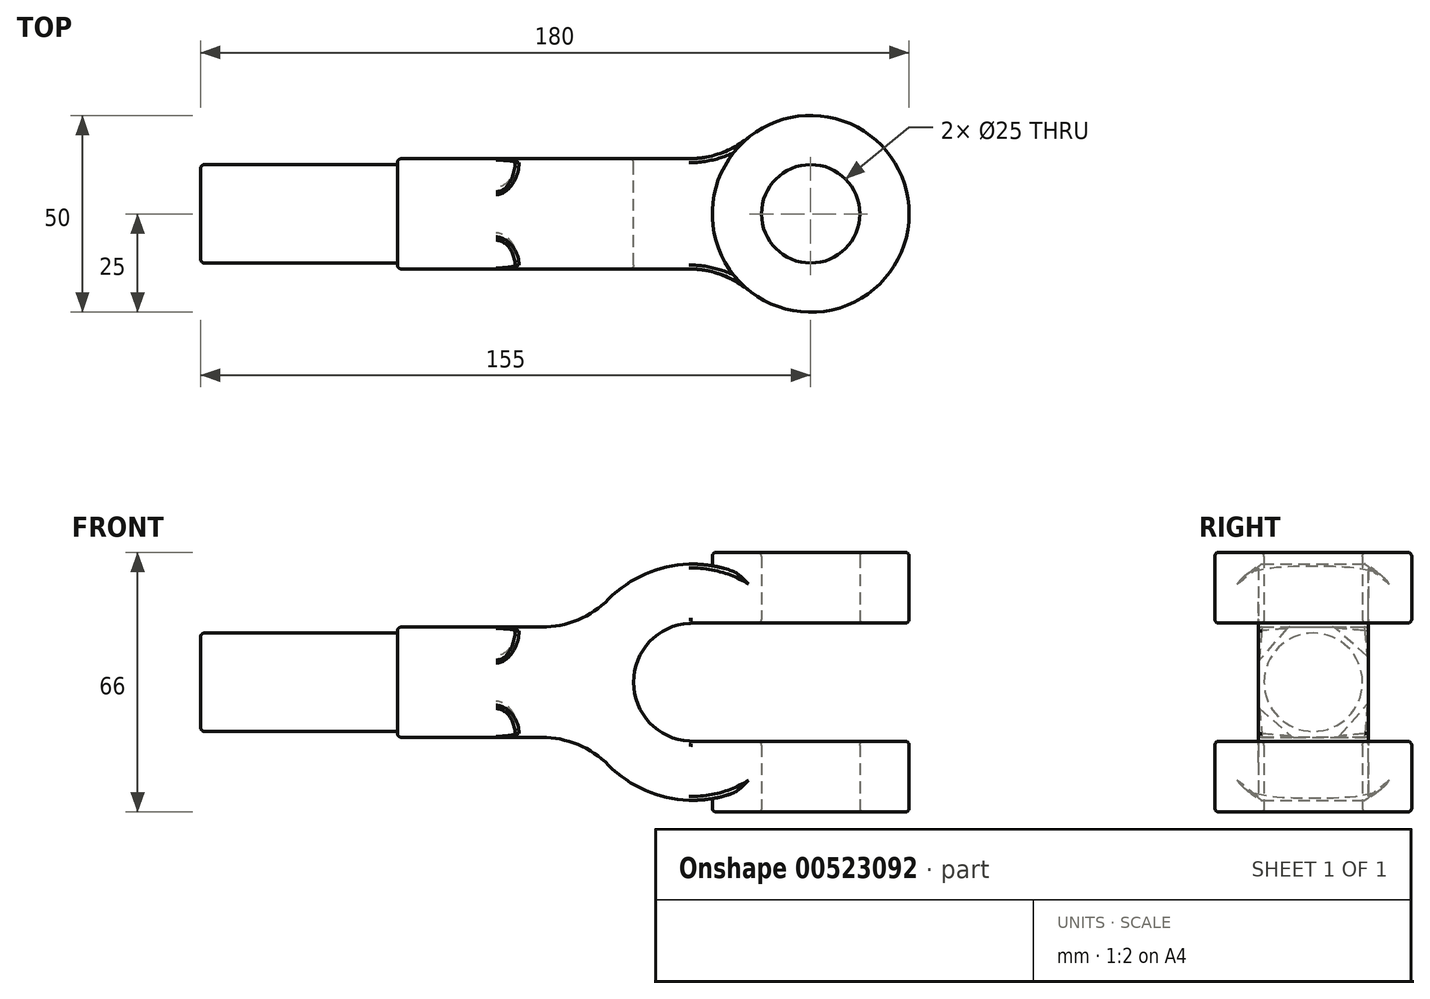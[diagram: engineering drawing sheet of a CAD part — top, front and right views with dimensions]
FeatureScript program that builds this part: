
annotation { "Feature Type Name" : "Feature", "Feature Type Description" : "" }
export const myFeature = defineFeature(function(context is Context, id is Id, definition is map)
    precondition{}
    {
        {
            var Q0;
            Q0=qCreatedBy(makeId("Top.planeOp"),FACE);
            var sketch = newSketch(context, id + "F0", { "sketchPlane" : qUnion([Q0])});
            skCircle(sketch, "E0", {"center": v(0, 0) * mm, "radius": 25 * mm});
            skSolve(sketch);
        }
        {
            var Q0;
            Q0 = qSketchRegion(id + "F0", true);
            extrude(context, id + "F1", {"entities" : qUnion([Q0]), "endBound" : BoundingType.SYMMETRIC, "depth" : 66 * mm, "offsetDistance" : 25 * mm});
        }
        {
            var Q0;
            Q0=qCreatedBy(makeId("Front.planeOp"),FACE);
            var sketch = newSketch(context, id + "F2", { "sketchPlane" : qUnion([Q0])});
            skArc(sketch, "E1", {"start": v(-56.53, -14) * mm, "mid": v(0, 0) * mm, "end": v(-56.53, 14) * mm});
            skCircle(sketch, "E2", {"center": v(-30, 0) * mm, "radius": 15 * mm});
            skLineSegment(sketch, "E3.bottom", {"start": v(-75, 14) * mm, "end": v(-65, 14) * mm});
            skLineSegment(sketch, "E3.top", {"start": v(-75, -14) * mm, "end": v(-56.53, -14) * mm});
            skLineSegment(sketch, "E3.left", {"start": v(-75, 14) * mm, "end": v(-75, -14) * mm});
            skLineSegment(sketch, "E4", {"start": v(-65, 14) * mm, "end": v(-56.53, 14) * mm});
            skPoint(sketch, "E5.orphan", {"position": v(-55, 14) * mm});
            skSolve(sketch);
        }
        {
            var Q0;
            Q0 = qSketchRegion(id + "F2", true);
            extrude(context, id + "F3", {"entities" : qUnion([Q0]), "operationType" : NewBodyOperationType.ADD, "endBound" : BoundingType.SYMMETRIC, "depth" : 28 * mm, "offsetDistance" : 25 * mm});
        }
        {
            var Q0;
            Q0=makeQuery(id+"F3.opExtrude","SWEPT_FACE",FACE,{"disambiguationData":[OSD([sQuery(id+"F2.wireOp",EDGE,"E3.left")])]});
            extrude(context, id + "F4", {"entities" : qUnion([Q0]), "operationType" : NewBodyOperationType.ADD, "depth" : 30 * mm, "offsetDistance" : 25 * mm});
        }
        {
            var Q0;
            Q0=makeQuery(id+"F4.opExtrude","CAP_FACE",FACE,{"disambiguationData":[OSD([sQuery(id+"F2.wireOp",EDGE,"E3.left")])],"isStart":false});
            var sketch = newSketch(context, id + "F5", { "sketchPlane" : qUnion([Q0])});
            skCircle(sketch, "E6", {"center": v(0, 0) * mm, "radius": 12.5 * mm});
            skSolve(sketch);
        }
        {
            var Q0;
            Q0 = qSketchRegion(id + "F5", true);
            extrude(context, id + "F6", {"entities" : qUnion([Q0]), "operationType" : NewBodyOperationType.ADD, "depth" : 50 * mm, "offsetDistance" : 25 * mm});
        }
        {
            var Q0;
            Q0=qCreatedBy(makeId("Front.planeOp"),FACE);
            var sketch = newSketch(context, id + "F7", { "sketchPlane" : qUnion([Q0])});
            skLineSegment(sketch, "E7.bottom", {"start": v(-30, 15) * mm, "end": v(30, 15) * mm});
            skLineSegment(sketch, "E7.top", {"start": v(-30, -15) * mm, "end": v(30, -15) * mm});
            skLineSegment(sketch, "E7.left", {"start": v(-30, 15) * mm, "end": v(-30, -15) * mm});
            skLineSegment(sketch, "E7.right", {"start": v(30, 15) * mm, "end": v(30, -15) * mm});
            skPoint(sketch, "E7.middle", {"position": v(0, 0) * mm});
            skSolve(sketch);
        }
        {
            var Q0;
            Q0 = qSketchRegion(id + "F7", true);
            extrude(context, id + "F8", {"entities" : qUnion([Q0]), "operationType" : NewBodyOperationType.REMOVE, "endBound" : BoundingType.SYMMETRIC, "oppositeDirection" : true, "depth" : 60 * mm, "offsetDistance" : 25 * mm});
        }
        {
            var Q0;
            Q0=makeQuery(id+"F1.opExtrude","CAP_FACE",FACE,{"disambiguationData":[OSD([sQuery(id+"F0.wireOp",EDGE,"E0")])],"isStart":true});
            var sketch = newSketch(context, id + "F9", { "sketchPlane" : qUnion([Q0])});
            skCircle(sketch, "E8", {"center": v(0, 0) * mm, "radius": 12.5 * mm});
            skSolve(sketch);
        }
        {
            var Q0;
            Q0 = qSketchRegion(id + "F9", true);
            extrude(context, id + "F10", {"entities" : qUnion([Q0]), "operationType" : NewBodyOperationType.REMOVE, "endBound" : BoundingType.THROUGH_ALL, "oppositeDirection" : true, "depth" : 25 * mm, "offsetDistance" : 25 * mm});
        }
        {
            var Q0;
            Q0=makeQuery(id+"F3.boolean.opBoolean","INTERSECT",EDGE,{"disambiguationData":[OD(1.0)],"derivedFrom":[makeQuery(id+"F1.opExtrude","SWEPT_FACE",FACE,{"disambiguationData":[OSD([sQuery(id+"F0.wireOp",EDGE,"E0")])]}),makeQuery(id+"F3.opExtrude","CAP_FACE",FACE,{"disambiguationData":[OSD([sQuery(id+"F2.wireOp",EDGE,"E1"),sQuery(id+"F2.wireOp",EDGE,"E2"),sQuery(id+"F2.wireOp",EDGE,"E3.bottom"),sQuery(id+"F2.wireOp",EDGE,"E3.top"),sQuery(id+"F2.wireOp",EDGE,"E3.left"),sQuery(id+"F2.wireOp",EDGE,"E4")])],"isStart":false})]});
            fillet(context, id + "F11", {"entities" : qUnion([Q0]), "radius" : 24 * mm, "tangentPropagation" : true, "allowEdgeOverflow" : false});
        }
        {
            var Q0;
            Q0=makeQuery(id+"F3.boolean.opBoolean","INTERSECT",EDGE,{"disambiguationData":[OD(0.0)],"derivedFrom":[makeQuery(id+"F1.opExtrude","SWEPT_FACE",FACE,{"disambiguationData":[OSD([sQuery(id+"F0.wireOp",EDGE,"E0")])]}),makeQuery(id+"F3.opExtrude","CAP_FACE",FACE,{"disambiguationData":[OSD([sQuery(id+"F2.wireOp",EDGE,"E1"),sQuery(id+"F2.wireOp",EDGE,"E2"),sQuery(id+"F2.wireOp",EDGE,"E3.bottom"),sQuery(id+"F2.wireOp",EDGE,"E3.top"),sQuery(id+"F2.wireOp",EDGE,"E3.left"),sQuery(id+"F2.wireOp",EDGE,"E4")])],"isStart":false})]});
            fillet(context, id + "F12", {"entities" : qUnion([Q0]), "radius" : 24 * mm, "tangentPropagation" : true, "allowEdgeOverflow" : false});
        }
        {
            var Q0;
            Q0=makeQuery(id+"F3.boolean.opBoolean","INTERSECT",EDGE,{"disambiguationData":[OD(0.0)],"derivedFrom":[makeQuery(id+"F1.opExtrude","SWEPT_FACE",FACE,{"disambiguationData":[OSD([sQuery(id+"F0.wireOp",EDGE,"E0")])]}),makeQuery(id+"F3.opExtrude","CAP_FACE",FACE,{"disambiguationData":[OSD([sQuery(id+"F2.wireOp",EDGE,"E1"),sQuery(id+"F2.wireOp",EDGE,"E2"),sQuery(id+"F2.wireOp",EDGE,"E3.bottom"),sQuery(id+"F2.wireOp",EDGE,"E3.top"),sQuery(id+"F2.wireOp",EDGE,"E3.left"),sQuery(id+"F2.wireOp",EDGE,"E4")])],"isStart":true})]});
            fillet(context, id + "F13", {"entities" : qUnion([Q0]), "radius" : 24 * mm, "tangentPropagation" : true, "allowEdgeOverflow" : false});
        }
        {
            var Q0;
            Q0=makeQuery(id+"F3.boolean.opBoolean","INTERSECT",EDGE,{"disambiguationData":[OD(1.0)],"derivedFrom":[makeQuery(id+"F1.opExtrude","SWEPT_FACE",FACE,{"disambiguationData":[OSD([sQuery(id+"F0.wireOp",EDGE,"E0")])]}),makeQuery(id+"F3.opExtrude","CAP_FACE",FACE,{"disambiguationData":[OSD([sQuery(id+"F2.wireOp",EDGE,"E1"),sQuery(id+"F2.wireOp",EDGE,"E2"),sQuery(id+"F2.wireOp",EDGE,"E3.bottom"),sQuery(id+"F2.wireOp",EDGE,"E3.top"),sQuery(id+"F2.wireOp",EDGE,"E3.left"),sQuery(id+"F2.wireOp",EDGE,"E4")])],"isStart":true})]});
            fillet(context, id + "F14", {"entities" : qUnion([Q0]), "radius" : 24 * mm, "tangentPropagation" : true, "allowEdgeOverflow" : false});
        }
        {
            var Q0;
            Q0=makeQuery(id+"F3.opExtrude","SWEPT_EDGE",EDGE,{"disambiguationData":[OSD([sQuery(id+"F2.wireOp",EDGE,"E1"),sQuery(id+"F2.wireOp",EDGE,"E3.top")])]});
            fillet(context, id + "F15", {"entities" : qUnion([Q0]), "radius" : 24 * mm, "tangentPropagation" : true, "allowEdgeOverflow" : false});
        }
        {
            var Q0;
            Q0=makeQuery(id+"F3.opExtrude","SWEPT_EDGE",EDGE,{"disambiguationData":[OSD([sQuery(id+"F2.wireOp",EDGE,"E1"),sQuery(id+"F2.wireOp",EDGE,"E4")])]});
            fillet(context, id + "F16", {"entities" : qUnion([Q0]), "radius" : 24 * mm, "tangentPropagation" : true, "allowEdgeOverflow" : false});
        }
        {
            var Q0;
            Q0=makeQuery(id+"F4.opExtrude","CAP_FACE",FACE,{"disambiguationData":[OSD([sQuery(id+"F2.wireOp",EDGE,"E3.left")])],"isStart":false});
            var sketch = newSketch(context, id + "F17", { "sketchPlane" : qUnion([Q0])});
            skLineSegment(sketch, "E9", {"start": v(5.24, -14) * mm, "end": v(-6.37, -14) * mm});
            skLineSegment(sketch, "E10", {"start": v(-6.37, -14) * mm, "end": v(-14, -5.24) * mm});
            skLineSegment(sketch, "E11", {"start": v(-14, -5.24) * mm, "end": v(-14, 6.37) * mm});
            skLineSegment(sketch, "E12", {"start": v(-14, 6.37) * mm, "end": v(-5.24, 14) * mm});
            skLineSegment(sketch, "E13", {"start": v(-5.24, 14) * mm, "end": v(6.37, 14) * mm});
            skLineSegment(sketch, "E14", {"start": v(6.37, 14) * mm, "end": v(14, 5.24) * mm});
            skLineSegment(sketch, "E15", {"start": v(14, 5.24) * mm, "end": v(14, -6.37) * mm});
            skLineSegment(sketch, "E16", {"start": v(14, -6.37) * mm, "end": v(5.24, -14) * mm});
            skLineSegment(sketch, "E17.bottom", {"start": v(-18.8, -19.26) * mm, "end": v(18.8, -19.26) * mm});
            skLineSegment(sketch, "E17.top", {"start": v(-18.8, 19.26) * mm, "end": v(18.8, 19.26) * mm});
            skLineSegment(sketch, "E17.left", {"start": v(-18.8, -19.26) * mm, "end": v(-18.8, 19.26) * mm});
            skLineSegment(sketch, "E17.right", {"start": v(18.8, -19.26) * mm, "end": v(18.8, 19.26) * mm});
            skPoint(sketch, "E17.middle", {"position": v(0, 0) * mm});
            skSolve(sketch);
        }
        {
            var Q0;
            Q0 = qSketchRegion(id + "F17", true);
            extrude(context, id + "F18", {"entities" : qUnion([Q0]), "operationType" : NewBodyOperationType.REMOVE, "oppositeDirection" : true, "depth" : 30 * mm, "offsetDistance" : 25 * mm});
        }
        {
            var Q0;
            Q0=makeQuery(id+"F18.boolean.opBoolean","COPY",EDGE,{"derivedFrom":makeQuery(id+"F18.opExtrude","CAP_EDGE",EDGE,{"disambiguationData":[OSD([sQuery(id+"F17.wireOp",EDGE,"E16")])],"isStart":false})});
            fillet(context, id + "F19", {"entities" : qUnion([Q0]), "radius" : 5 * mm, "tangentPropagation" : true, "allowEdgeOverflow" : false});
        }
        {
            var Q0;
            Q0=makeQuery(id+"F18.boolean.opBoolean","COPY",EDGE,{"derivedFrom":makeQuery(id+"F18.opExtrude","CAP_EDGE",EDGE,{"disambiguationData":[OSD([sQuery(id+"F17.wireOp",EDGE,"E10")])],"isStart":false})});
            fillet(context, id + "F20", {"entities" : qUnion([Q0]), "radius" : 5 * mm, "tangentPropagation" : true, "allowEdgeOverflow" : false});
        }
        {
            var Q0;
            Q0=makeQuery(id+"F18.boolean.opBoolean","COPY",EDGE,{"derivedFrom":makeQuery(id+"F18.opExtrude","CAP_EDGE",EDGE,{"disambiguationData":[OSD([sQuery(id+"F17.wireOp",EDGE,"E12")])],"isStart":false})});
            fillet(context, id + "F21", {"entities" : qUnion([Q0]), "radius" : 5 * mm, "tangentPropagation" : true, "allowEdgeOverflow" : false});
        }
        {
            var Q0;
            Q0=makeQuery(id+"F18.boolean.opBoolean","COPY",EDGE,{"derivedFrom":makeQuery(id+"F18.opExtrude","CAP_EDGE",EDGE,{"disambiguationData":[OSD([sQuery(id+"F17.wireOp",EDGE,"E14")])],"isStart":false})});
            fillet(context, id + "F22", {"entities" : qUnion([Q0]), "radius" : 5 * mm, "tangentPropagation" : true, "allowEdgeOverflow" : false});
        }
        {
            var Q0;
            {var subQ0=sQuery(id+"F2.wireOp",EDGE,"E3.left");Q0=makeQuery(id+"F4.boolean.opBoolean","MERGE",FACE,{"derivedFrom":[makeQuery(id+"F3.opExtrude","CAP_FACE",FACE,{"disambiguationData":[OSD([sQuery(id+"F2.wireOp",EDGE,"E1"),sQuery(id+"F2.wireOp",EDGE,"E2"),sQuery(id+"F2.wireOp",EDGE,"E3.bottom"),sQuery(id+"F2.wireOp",EDGE,"E3.top"),subQ0,sQuery(id+"F2.wireOp",EDGE,"E4")])],"isStart":false}),makeQuery(id+"F4.opExtrude","SWEPT_FACE",FACE,{"disambiguationData":[OSD([subQ0]),TDD([makeQuery(id+"F3.opExtrude","CAP_EDGE",EDGE,{"disambiguationData":[OSD([subQ0])],"isStart":false})])]})]});}
            var Q1;
            {var subQ0=sQuery(id+"F2.wireOp",EDGE,"E3.top");Q1=makeQuery(id+"F4.boolean.opBoolean","MERGE",FACE,{"derivedFrom":[makeQuery(id+"F3.opExtrude","SWEPT_FACE",FACE,{"disambiguationData":[OSD([subQ0])]}),makeQuery(id+"F4.opExtrude","SWEPT_FACE",FACE,{"disambiguationData":[OSD([subQ0,sQuery(id+"F2.wireOp",EDGE,"E3.left")])]})]});}
            var Q2;
            {var subQ0=sQuery(id+"F2.wireOp",EDGE,"E3.left");Q2=makeQuery(id+"F4.boolean.opBoolean","MERGE",FACE,{"derivedFrom":[makeQuery(id+"F3.opExtrude","CAP_FACE",FACE,{"disambiguationData":[OSD([sQuery(id+"F2.wireOp",EDGE,"E1"),sQuery(id+"F2.wireOp",EDGE,"E2"),sQuery(id+"F2.wireOp",EDGE,"E3.bottom"),sQuery(id+"F2.wireOp",EDGE,"E3.top"),subQ0,sQuery(id+"F2.wireOp",EDGE,"E4")])],"isStart":true}),makeQuery(id+"F4.opExtrude","SWEPT_FACE",FACE,{"disambiguationData":[OSD([subQ0]),TDD([makeQuery(id+"F3.opExtrude","CAP_EDGE",EDGE,{"disambiguationData":[OSD([subQ0])],"isStart":true})])]})]});}
            var Q3;
            {var subQ0=sQuery(id+"F2.wireOp",EDGE,"E3.bottom");Q3=makeQuery(id+"F4.boolean.opBoolean","MERGE",FACE,{"derivedFrom":[makeQuery(id+"F3.opExtrude","SWEPT_FACE",FACE,{"disambiguationData":[OSD([subQ0,sQuery(id+"F2.wireOp",EDGE,"E4")])]}),makeQuery(id+"F4.opExtrude","SWEPT_FACE",FACE,{"disambiguationData":[OSD([subQ0,sQuery(id+"F2.wireOp",EDGE,"E3.left")])]})]});}
            var Q4;
            Q4=makeQuery(id+"F1.opExtrude","CAP_FACE",FACE,{"disambiguationData":[OSD([sQuery(id+"F0.wireOp",EDGE,"E0")])],"isStart":false});
            var Q5;
            Q5=makeQuery(id+"F1.opExtrude","CAP_FACE",FACE,{"disambiguationData":[OSD([sQuery(id+"F0.wireOp",EDGE,"E0")])],"isStart":true});
            var Q6;
            Q6=makeQuery(id+"F8.boolean.opBoolean","COPY",FACE,{"derivedFrom":makeQuery(id+"F8.opExtrude","SWEPT_FACE",FACE,{"disambiguationData":[OSD([sQuery(id+"F7.wireOp",EDGE,"E7.bottom")])]})});
            var Q7;
            Q7=makeQuery(id+"F8.boolean.opBoolean","COPY",FACE,{"derivedFrom":makeQuery(id+"F8.opExtrude","SWEPT_FACE",FACE,{"disambiguationData":[OSD([sQuery(id+"F7.wireOp",EDGE,"E7.top")])]})});
            var Q8;
            Q8=makeQuery(id+"F18.boolean.opBoolean","COPY",FACE,{"derivedFrom":makeQuery(id+"F18.opExtrude","SWEPT_FACE",FACE,{"disambiguationData":[OSD([sQuery(id+"F17.wireOp",EDGE,"E16")])]})});
            var Q9;
            Q9=makeQuery(id+"F18.boolean.opBoolean","COPY",FACE,{"derivedFrom":makeQuery(id+"F18.opExtrude","SWEPT_FACE",FACE,{"disambiguationData":[OSD([sQuery(id+"F17.wireOp",EDGE,"E10")])]})});
            var Q10;
            Q10=makeQuery(id+"F18.boolean.opBoolean","COPY",FACE,{"derivedFrom":makeQuery(id+"F18.opExtrude","SWEPT_FACE",FACE,{"disambiguationData":[OSD([sQuery(id+"F17.wireOp",EDGE,"E12")])]})});
            var Q11;
            Q11=makeQuery(id+"F18.boolean.opBoolean","COPY",FACE,{"derivedFrom":makeQuery(id+"F18.opExtrude","SWEPT_FACE",FACE,{"disambiguationData":[OSD([sQuery(id+"F17.wireOp",EDGE,"E14")])]})});
            var Q12;
            Q12=makeQuery(id+"F6.opExtrude","CAP_FACE",FACE,{"disambiguationData":[OSD([sQuery(id+"F5.wireOp",EDGE,"E6")])],"isStart":false});
            fillet(context, id + "F23", {"entities" : qUnion([Q0, Q1, Q2, Q3, Q4, Q5, Q6, Q7, Q8, Q9, Q10, Q11, Q12]), "radius" : 1 * mm, "tangentPropagation" : true, "allowEdgeOverflow" : false});
        }
    });
